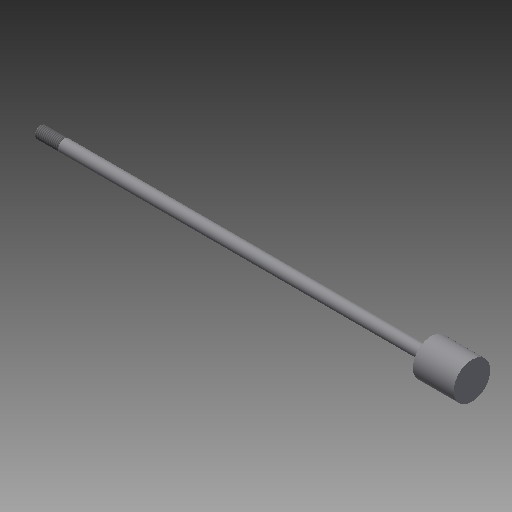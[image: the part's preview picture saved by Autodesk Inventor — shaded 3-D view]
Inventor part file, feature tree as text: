
AUTODESK INVENTOR PART (.ipt)
format: ipt  version: 2019 (Build 230136000, 136)  size: 151,552 bytes
history: native  units: in
note: dims shown in document units (in); Inventor stores cm internally (conversion verified against a paired STEP export)
features: other x84, revolve x3, sketch x3, thread x1
ambient origin geometry x8: Origin, YZ Plane, XZ Plane, XY Plane, X Axis, Y Axis, Z Axis, Center Point
bodies: Solid1 (feature_tree)
feature tree (91):
  revolve  "Revolution1"  Angle=360.0deg
  revolve  "Revolution2"  Angle=360.0deg
  thread  "Thread1"  [1 undecoded]
  revolve  "Revolution3"  [1 undecoded]
  other  "dia1_XY"
  other  "dia1_YZ"
  other  "dia1_ZX"
  other  "dia1_X"
  other  "dia1_Y"
  other  "dia1_Z"
  other  "dia1_Center"
  other  "dia12_XY"
  other  "dia12_YZ"
  other  "dia12_ZX"
  other  "dia12_X"
  other  "dia12_Y"
  other  "dia12_Z"
  other  "dia12_Center"
  other  "dia2_XY"
  other  "dia2_YZ"
  other  "dia2_ZX"
  other  "dia2_X"
  other  "dia2_Y"
  other  "dia2_Z"
  other  "dia2_Center"
  other  "dia22_XY"
  other  "dia22_YZ"
  other  "dia22_ZX"
  other  "dia22_X"
  other  "dia22_Y"
  other  "dia22_Z"
  other  "dia22_Center"
  other  "hh1_XY"
  other  "hh1_YZ"
  other  "hh1_ZX"
  other  "hh1_X"
  other  "hh1_Y"
  other  "hh1_Z"
  other  "hh1_Center"
  other  "hh2_XY"
  other  "hh2_YZ"
  other  "hh2_ZX"
  other  "hh2_X"
  other  "hh2_Y"
  other  "hh2_Z"
  other  "hh2_Center"
  other  "rl1_XY"
  other  "rl1_YZ"
  other  "rl1_ZX"
  other  "rl1_X"
  other  "rl1_Y"
  other  "rl1_Z"
  other  "rl1_Center"
  other  "rl2_XY"
  other  "rl2_YZ"
  other  "rl2_ZX"
  other  "rl2_X"
  other  "rl2_Y"
  other  "rl2_Z"
  other  "rl2_Center"
  other  "rod_cp_XY"
  other  "rod_cp_YZ"
  other  "rod_cp_ZX"
  other  "rod_cp_X"
  other  "rod_cp_Y"
  other  "rod_cp_Z"
  other  "rod_cp_Center"
  other  "thd1_XY"
  other  "thd1_YZ"
  other  "thd1_ZX"
  other  "thd1_X"
  other  "thd1_Y"
  other  "thd1_Z"
  other  "thd1_Center"
  other  "thd2_XY"
  other  "thd2_YZ"
  other  "thd2_ZX"
  other  "thd2_X"
  other  "thd2_Y"
  other  "thd2_Z"
  other  "thd2_Center"
  other  "to_rod_clevis_XY"
  other  "to_rod_clevis_YZ"
  other  "to_rod_clevis_ZX"
  other  "to_rod_clevis_X"
  other  "to_rod_clevis_Y"
  other  "to_rod_clevis_Z"
  other  "to_rod_clevis_Center"
  sketch  "Sketch_1"  dims[d0=360.0deg d1=360.0deg]
  sketch  "Sketch_3"  dims[d2=0.4787in d3=0.0in d4=360.0deg]
  sketch  "Sketch_30"  dims[d5=0.0in d6=0.0in d7=0.0in d8=0.0in d9=0.0in]
note: 2 required parameter values undecoded (feature->parameter linkage not recoverable at this tier; creation-order binding heuristic only, values carry confidence <= 0.55)
